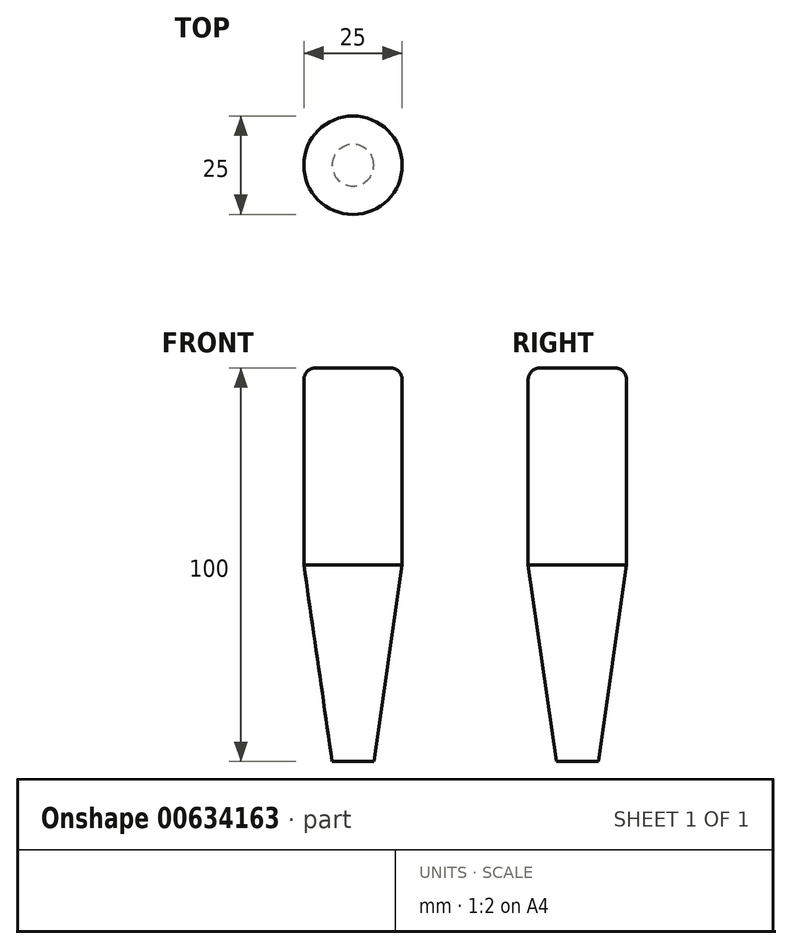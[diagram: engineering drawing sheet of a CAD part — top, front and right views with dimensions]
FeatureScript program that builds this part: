
annotation { "Feature Type Name" : "Feature", "Feature Type Description" : "" }
export const myFeature = defineFeature(function(context is Context, id is Id, definition is map)
    precondition{}
    {
        {
            var Q0;
            Q0=qCreatedBy(makeId("Front.planeOp"),FACE);
            var sketch = newSketch(context, id + "F0", { "sketchPlane" : qUnion([Q0])});
            skLineSegment(sketch, "E0", {"start": v(0, 0) * mm, "end": v(0, 100) * mm});
            skLineSegment(sketch, "E1", {"start": v(0, 100) * mm, "end": v(-9.5, 100) * mm});
            skLineSegment(sketch, "E2", {"start": v(-12.5, 97) * mm, "end": v(-12.5, 50) * mm});
            skLineSegment(sketch, "E3", {"start": v(-12.5, 50) * mm, "end": v(-5.3, 0) * mm});
            skLineSegment(sketch, "E4", {"start": v(-5.3, 0) * mm, "end": v(0, 0) * mm});
            skPoint(sketch, "E5.visualSharp", {"position": v(-12.5, 100) * mm});
            skArc(sketch, "E5.filletArc", {"start": v(-9.5, 100) * mm, "mid": v(-11.62, 99.12) * mm, "end": v(-12.5, 97) * mm});
            skSolve(sketch);
        }
        {
            var Q0;
            Q0=makeQuery(id+"F0.imprint","IMPRINT",FACE,{"disambiguationData":[TD([[makeQuery(id+"F0.imprint","IMPRINT",EDGE,{"derivedFrom":sQuery(id+"F0.wireOp",EDGE,"E0")}),1.0]])]});
            var Q1;
            Q1=sQuery(id+"F0.wireOp",EDGE,"E0");
            revolve(context, id + "F1", {"entities" : qUnion([Q0]), "axis" : qUnion([Q1]), "revolveType" : RevolveType.FULL});
        }
    });
